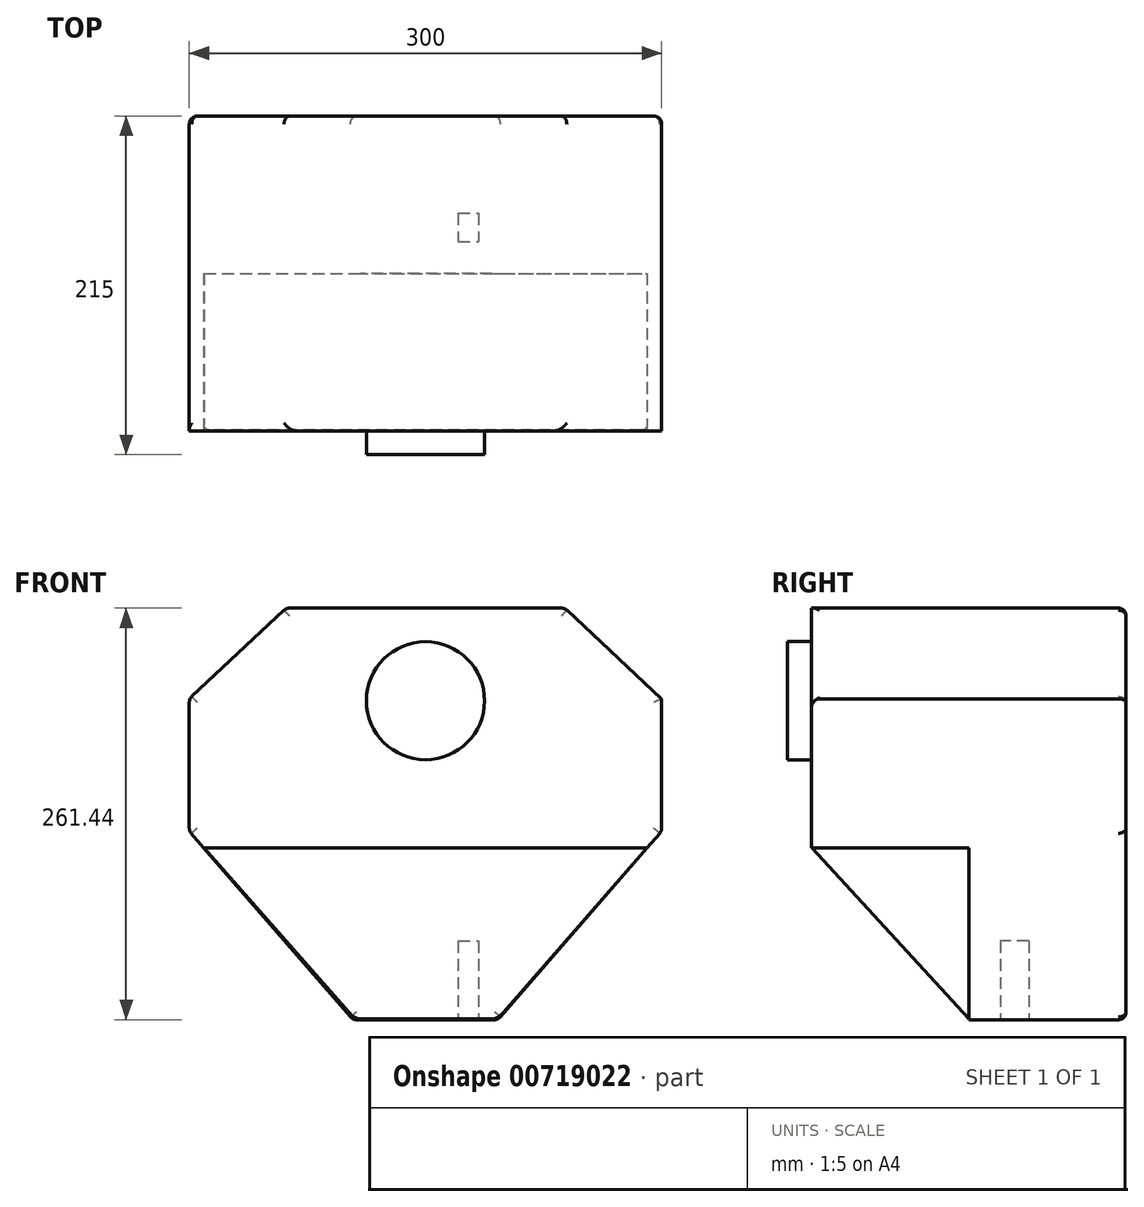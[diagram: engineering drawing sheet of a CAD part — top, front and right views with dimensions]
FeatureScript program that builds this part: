
annotation { "Feature Type Name" : "Feature", "Feature Type Description" : "" }
export const myFeature = defineFeature(function(context is Context, id is Id, definition is map)
    precondition{}
    {
        {
            var Q0;
            Q0=qCreatedBy(makeId("Front.planeOp"),FACE);
            var sketch = newSketch(context, id + "F0", { "sketchPlane" : qUnion([Q0])});
            skLineSegment(sketch, "E0.bottom", {"start": v(-150, -42) * mm, "end": v(150, -42) * mm});
            skLineSegment(sketch, "E0.top", {"start": v(-150, 42) * mm, "end": v(150, 42) * mm});
            skLineSegment(sketch, "E0.left", {"start": v(-150, -42) * mm, "end": v(-150, 42) * mm});
            skLineSegment(sketch, "E0.right", {"start": v(150, -42) * mm, "end": v(150, 42) * mm});
            skPoint(sketch, "E0.middle", {"position": v(0, 0) * mm});
            skLineSegment(sketch, "E1.bottom", {"start": v(-88.3, -15.66) * mm, "end": v(88.3, -15.66) * mm});
            skLineSegment(sketch, "E1.top", {"start": v(-88.3, 99.65) * mm, "end": v(88.3, 99.65) * mm});
            skLineSegment(sketch, "E1.left", {"start": v(-88.3, -15.66) * mm, "end": v(-88.3, 99.65) * mm});
            skLineSegment(sketch, "E1.right", {"start": v(88.3, -15.66) * mm, "end": v(88.3, 99.65) * mm});
            skPoint(sketch, "E1.middle", {"position": v(0, 42) * mm});
            skLineSegment(sketch, "E2.bottom", {"start": v(-46.14, -161.8) * mm, "end": v(46.14, -161.8) * mm});
            skLineSegment(sketch, "E2.top", {"start": v(-46.14, 77.8) * mm, "end": v(46.14, 77.8) * mm});
            skLineSegment(sketch, "E2.left", {"start": v(-46.14, -161.8) * mm, "end": v(-46.14, 77.8) * mm});
            skLineSegment(sketch, "E2.right", {"start": v(46.14, -161.8) * mm, "end": v(46.14, 77.8) * mm});
            skPoint(sketch, "E2.middle", {"position": v(0, -42) * mm});
            skLineSegment(sketch, "E3", {"start": v(-150, -42) * mm, "end": v(-46.14, -161.8) * mm});
            skLineSegment(sketch, "E4", {"start": v(46.14, -161.8) * mm, "end": v(150, -42) * mm});
            skLineSegment(sketch, "E5", {"start": v(-150, 42) * mm, "end": v(-88.3, 99.65) * mm});
            skLineSegment(sketch, "E6", {"start": v(150, 42) * mm, "end": v(88.3, 99.65) * mm});
            skSolve(sketch);
        }
        {
            var Q0;
            {var subQ0=sQuery(id+"F0.wireOp",EDGE,"E2.left");var subQ1=sQuery(id+"F0.wireOp",EDGE,"E0.top");var subQ2=makeQuery(id+"F0.imprint","INTERSECT",VERTEX,{"derivedFrom":[subQ1,subQ0]});Q0=makeQuery(id+"F0.imprint","IMPRINT",FACE,{"disambiguationData":[TD([[makeQuery(id+"F0.imprint","IMPRINT",EDGE,{"disambiguationData":[TD([[subQ2,-1.0]])],"derivedFrom":subQ1}),-1.0]])]});}
            var Q1;
            {var subQ0=sQuery(id+"F0.wireOp",EDGE,"E1.left");var subQ1=sQuery(id+"F0.wireOp",EDGE,"E0.top");var subQ2=makeQuery(id+"F0.imprint","INTERSECT",VERTEX,{"derivedFrom":[subQ1,subQ0]});Q1=makeQuery(id+"F0.imprint","IMPRINT",FACE,{"disambiguationData":[TD([[makeQuery(id+"F0.imprint","IMPRINT",EDGE,{"disambiguationData":[TD([[subQ2,-1.0]])],"derivedFrom":subQ1}),-1.0]])]});}
            var Q2;
            {var subQ0=sQuery(id+"F0.wireOp",EDGE,"E0.left");Q2=makeQuery(id+"F0.imprint","IMPRINT",FACE,{"disambiguationData":[TD([[makeQuery(id+"F0.imprint","IMPRINT",EDGE,{"derivedFrom":subQ0}),-1.0]])]});}
            var Q3;
            {var subQ0=sQuery(id+"F0.wireOp",EDGE,"E2.left");var subQ1=sQuery(id+"F0.wireOp",EDGE,"E0.bottom");var subQ2=makeQuery(id+"F0.imprint","INTERSECT",VERTEX,{"derivedFrom":[subQ1,subQ0]});Q3=makeQuery(id+"F0.imprint","IMPRINT",FACE,{"disambiguationData":[TD([[makeQuery(id+"F0.imprint","IMPRINT",EDGE,{"disambiguationData":[TD([[subQ2,-1.0]])],"derivedFrom":subQ1}),1.0]])]});}
            var Q4;
            {var subQ0=sQuery(id+"F0.wireOp",EDGE,"E0.right");Q4=makeQuery(id+"F0.imprint","IMPRINT",FACE,{"disambiguationData":[TD([[makeQuery(id+"F0.imprint","IMPRINT",EDGE,{"derivedFrom":subQ0}),1.0]])]});}
            var Q5;
            {var subQ0=sQuery(id+"F0.wireOp",EDGE,"E2.right");var subQ1=sQuery(id+"F0.wireOp",EDGE,"E0.top");var subQ2=makeQuery(id+"F0.imprint","INTERSECT",VERTEX,{"derivedFrom":[subQ1,subQ0]});Q5=makeQuery(id+"F0.imprint","IMPRINT",FACE,{"disambiguationData":[TD([[makeQuery(id+"F0.imprint","IMPRINT",EDGE,{"disambiguationData":[TD([[subQ2,-1.0]])],"derivedFrom":subQ1}),-1.0]])]});}
            var Q6;
            {var subQ0=sQuery(id+"F0.wireOp",EDGE,"E3");Q6=makeQuery(id+"F0.imprint","IMPRINT",FACE,{"disambiguationData":[TD([[makeQuery(id+"F0.imprint","IMPRINT",EDGE,{"derivedFrom":subQ0}),1.0]])]});}
            var Q7;
            {var subQ5=sQuery(id+"F0.wireOp",EDGE,"E2.bottom");Q7=makeQuery(id+"F0.imprint","IMPRINT",FACE,{"disambiguationData":[TD([[makeQuery(id+"F0.imprint","IMPRINT",EDGE,{"derivedFrom":subQ5}),1.0]])]});}
            var Q8;
            {var subQ0=sQuery(id+"F0.wireOp",EDGE,"E4");Q8=makeQuery(id+"F0.imprint","IMPRINT",FACE,{"disambiguationData":[TD([[makeQuery(id+"F0.imprint","IMPRINT",EDGE,{"derivedFrom":subQ0}),1.0]])]});}
            var Q9;
            {var subQ1=sQuery(id+"F0.wireOp",EDGE,"E1.top");Q9=makeQuery(id+"F0.imprint","IMPRINT",FACE,{"disambiguationData":[TD([[makeQuery(id+"F0.imprint","IMPRINT",EDGE,{"derivedFrom":subQ1}),-1.0]])]});}
            var Q10;
            {var subQ5=sQuery(id+"F0.wireOp",EDGE,"E2.top");Q10=makeQuery(id+"F0.imprint","IMPRINT",FACE,{"disambiguationData":[TD([[makeQuery(id+"F0.imprint","IMPRINT",EDGE,{"derivedFrom":subQ5}),-1.0]])]});}
            var Q11;
            {var subQ0=sQuery(id+"F0.wireOp",EDGE,"E5");Q11=makeQuery(id+"F0.imprint","IMPRINT",FACE,{"disambiguationData":[TD([[makeQuery(id+"F0.imprint","IMPRINT",EDGE,{"derivedFrom":subQ0}),-1.0]])]});}
            var Q12;
            {var subQ0=sQuery(id+"F0.wireOp",EDGE,"E6");Q12=makeQuery(id+"F0.imprint","IMPRINT",FACE,{"disambiguationData":[TD([[makeQuery(id+"F0.imprint","IMPRINT",EDGE,{"derivedFrom":subQ0}),1.0]])]});}
            extrude(context, id + "F1", {"entities" : qUnion([Q0, Q1, Q2, Q3, Q4, Q5, Q6, Q7, Q8, Q9, Q10, Q11, Q12]), "depth" : 100 * mm, "offsetDistance" : 25 * mm, "hasSecondDirection" : true, "secondDirectionOppositeDirection" : true, "secondDirectionDepth" : 100 * mm});
        }
        {
            var Q0;
            Q0=makeQuery(id+"F1.opExtrude","CAP_FACE",FACE,{"disambiguationData":[OSD([sQuery(id+"F0.wireOp",EDGE,"E0.left"),sQuery(id+"F0.wireOp",EDGE,"E0.right"),sQuery(id+"F0.wireOp",EDGE,"E1.top"),sQuery(id+"F0.wireOp",EDGE,"E2.bottom"),sQuery(id+"F0.wireOp",EDGE,"E3"),sQuery(id+"F0.wireOp",EDGE,"E4"),sQuery(id+"F0.wireOp",EDGE,"E5"),sQuery(id+"F0.wireOp",EDGE,"E6")])],"isStart":false});
            var sketch = newSketch(context, id + "F2", { "sketchPlane" : qUnion([Q0])});
            skLineSegment(sketch, "E7", {"start": v(-140.78, -52.63) * mm, "end": v(140.78, -52.63) * mm});
            skLineSegment(sketch, "E8", {"start": v(140.78, -52.63) * mm, "end": v(46.14, -161.8) * mm});
            skLineSegment(sketch, "E9", {"start": v(46.14, -161.8) * mm, "end": v(-46.14, -161.8) * mm});
            skLineSegment(sketch, "E10", {"start": v(-46.14, -161.8) * mm, "end": v(-140.78, -52.63) * mm});
            skSolve(sketch);
        }
        {
            var Q0;
            Q0 = qSketchRegion(id + "F2", true);
            extrude(context, id + "F3", {"entities" : qUnion([Q0]), "operationType" : NewBodyOperationType.REMOVE, "oppositeDirection" : true, "depth" : 100 * mm, "offsetDistance" : 25 * mm});
        }
        {
            var Q0;
            Q0=qCreatedBy(makeId("Right.planeOp"),FACE);
            var sketch = newSketch(context, id + "F4", { "sketchPlane" : qUnion([Q0])});
            skLineSegment(sketch, "E11", {"start": v(0, -161.34) * mm, "end": v(-99.62, -52.57) * mm});
            skLineSegment(sketch, "E12", {"start": v(-99.62, -52.57) * mm, "end": v(0, -52.57) * mm});
            skLineSegment(sketch, "E13", {"start": v(0, -52.57) * mm, "end": v(0, -161.34) * mm});
            skSolve(sketch);
        }
        {
            var Q0;
            Q0=makeQuery(id+"F4.imprint","IMPRINT",FACE,{"disambiguationData":[TD([[makeQuery(id+"F4.imprint","IMPRINT",EDGE,{"derivedFrom":sQuery(id+"F4.wireOp",EDGE,"E11")}),-1.0]])]});
            extrude(context, id + "F5", {"entities" : qUnion([Q0]), "operationType" : NewBodyOperationType.ADD, "depth" : 150 * mm, "offsetDistance" : 25 * mm, "hasSecondDirection" : true, "secondDirectionOppositeDirection" : true, "secondDirectionDepth" : 150 * mm});
        }
        {
            var Q0;
            Q0=makeQuery(id+"F1.opExtrude","CAP_FACE",FACE,{"disambiguationData":[OSD([sQuery(id+"F0.wireOp",EDGE,"E0.left"),sQuery(id+"F0.wireOp",EDGE,"E0.right"),sQuery(id+"F0.wireOp",EDGE,"E1.top"),sQuery(id+"F0.wireOp",EDGE,"E2.bottom"),sQuery(id+"F0.wireOp",EDGE,"E3"),sQuery(id+"F0.wireOp",EDGE,"E4"),sQuery(id+"F0.wireOp",EDGE,"E5"),sQuery(id+"F0.wireOp",EDGE,"E6")])],"isStart":false});
            var sketch = newSketch(context, id + "F6", { "sketchPlane" : qUnion([Q0])});
            skLineSegment(sketch, "E14", {"start": v(-150, -42) * mm, "end": v(-44.71, -161.7) * mm});
            skLineSegment(sketch, "E15", {"start": v(-44.71, -161.7) * mm, "end": v(45.6, -161.7) * mm});
            skLineSegment(sketch, "E16", {"start": v(45.6, -161.7) * mm, "end": v(150, -42) * mm});
            skLineSegment(sketch, "E17", {"start": v(150, -42) * mm, "end": v(150, -161.7) * mm});
            skLineSegment(sketch, "E18", {"start": v(150, -161.7) * mm, "end": v(-150.56, -161.7) * mm});
            skLineSegment(sketch, "E19", {"start": v(-150.56, -161.7) * mm, "end": v(-150, -42) * mm});
            skSolve(sketch);
        }
        {
            var Q0;
            {var subQ1=sQuery(id+"F6.wireOp",EDGE,"E19");Q0=makeQuery(id+"F6.imprint","IMPRINT",FACE,{"disambiguationData":[TD([[makeQuery(id+"F6.imprint","IMPRINT",EDGE,{"derivedFrom":subQ1}),-1.0]])]});}
            var Q1;
            {var subQ1=sQuery(id+"F6.wireOp",EDGE,"E17");Q1=makeQuery(id+"F6.imprint","IMPRINT",FACE,{"disambiguationData":[TD([[makeQuery(id+"F6.imprint","IMPRINT",EDGE,{"derivedFrom":subQ1}),-1.0]])]});}
            extrude(context, id + "F7", {"entities" : qUnion([Q0, Q1]), "operationType" : NewBodyOperationType.REMOVE, "oppositeDirection" : true, "depth" : 100 * mm, "offsetDistance" : 25 * mm});
        }
        {
            var Q0;
            Q0=makeQuery(id+"F1.opExtrude","CAP_EDGE",EDGE,{"disambiguationData":[OSD([sQuery(id+"F0.wireOp",EDGE,"E1.top")])],"isStart":true});
            var Q1;
            Q1=makeQuery(id+"F1.opExtrude","CAP_EDGE",EDGE,{"disambiguationData":[OSD([sQuery(id+"F0.wireOp",EDGE,"E6")])],"isStart":true});
            var Q2;
            Q2=makeQuery(id+"F1.opExtrude","CAP_FACE",FACE,{"disambiguationData":[OSD([sQuery(id+"F0.wireOp",EDGE,"E0.left"),sQuery(id+"F0.wireOp",EDGE,"E0.right"),sQuery(id+"F0.wireOp",EDGE,"E1.top"),sQuery(id+"F0.wireOp",EDGE,"E2.bottom"),sQuery(id+"F0.wireOp",EDGE,"E3"),sQuery(id+"F0.wireOp",EDGE,"E4"),sQuery(id+"F0.wireOp",EDGE,"E5"),sQuery(id+"F0.wireOp",EDGE,"E6")])],"isStart":true});
            fillet(context, id + "F8", {"entities" : qUnion([Q0, Q1, Q2]), "radius" : 5 * mm, "tangentPropagation" : true, "allowEdgeOverflow" : false});
        }
        {
            var Q0;
            Q0=makeQuery(id+"F1.opExtrude","SWEPT_EDGE",EDGE,{"disambiguationData":[OSD([sQuery(id+"F0.wireOp",EDGE,"E0.bottom"),sQuery(id+"F0.wireOp",EDGE,"E0.right"),sQuery(id+"F0.wireOp",EDGE,"E4")])]});
            var Q1;
            Q1=makeQuery(id+"F7.boolean.opBoolean","INTERSECT",EDGE,{"derivedFrom":[makeQuery(id+"F5.opExtrude","SWEPT_FACE",FACE,{"disambiguationData":[OSD([sQuery(id+"F4.wireOp",EDGE,"E11")])]}),makeQuery(id+"F7.opExtrude","SWEPT_FACE",FACE,{"disambiguationData":[OSD([sQuery(id+"F6.wireOp",EDGE,"E16")])]})]});
            var Q2;
            Q2=makeQuery(id+"F1.opExtrude","SWEPT_EDGE",EDGE,{"disambiguationData":[OSD([sQuery(id+"F0.wireOp",EDGE,"E2.bottom"),sQuery(id+"F0.wireOp",EDGE,"E2.right"),sQuery(id+"F0.wireOp",EDGE,"E4")])]});
            var Q3;
            Q3=makeQuery(id+"F1.opExtrude","CAP_EDGE",EDGE,{"disambiguationData":[OSD([sQuery(id+"F0.wireOp",EDGE,"E6")])],"isStart":false});
            var Q4;
            Q4=makeQuery(id+"F1.opExtrude","SWEPT_EDGE",EDGE,{"disambiguationData":[OSD([sQuery(id+"F0.wireOp",EDGE,"E1.top"),sQuery(id+"F0.wireOp",EDGE,"E1.right"),sQuery(id+"F0.wireOp",EDGE,"E6")])]});
            var Q5;
            Q5=makeQuery(id+"F1.opExtrude","SWEPT_EDGE",EDGE,{"disambiguationData":[OSD([sQuery(id+"F0.wireOp",EDGE,"E1.top"),sQuery(id+"F0.wireOp",EDGE,"E1.left"),sQuery(id+"F0.wireOp",EDGE,"E5")])]});
            var Q6;
            Q6=makeQuery(id+"F1.opExtrude","CAP_EDGE",EDGE,{"disambiguationData":[OSD([sQuery(id+"F0.wireOp",EDGE,"E5")])],"isStart":false});
            var Q7;
            Q7=makeQuery(id+"F1.opExtrude","SWEPT_EDGE",EDGE,{"disambiguationData":[OSD([sQuery(id+"F0.wireOp",EDGE,"E0.top"),sQuery(id+"F0.wireOp",EDGE,"E0.left"),sQuery(id+"F0.wireOp",EDGE,"E5")])]});
            var Q8;
            Q8=makeQuery(id+"F1.opExtrude","SWEPT_EDGE",EDGE,{"disambiguationData":[OSD([sQuery(id+"F0.wireOp",EDGE,"E0.bottom"),sQuery(id+"F0.wireOp",EDGE,"E0.left"),sQuery(id+"F0.wireOp",EDGE,"E3")])]});
            var Q9;
            Q9=makeQuery(id+"F7.boolean.opBoolean","INTERSECT",EDGE,{"derivedFrom":[makeQuery(id+"F5.opExtrude","SWEPT_FACE",FACE,{"disambiguationData":[OSD([sQuery(id+"F4.wireOp",EDGE,"E11")])]}),makeQuery(id+"F7.opExtrude","SWEPT_FACE",FACE,{"disambiguationData":[OSD([sQuery(id+"F6.wireOp",EDGE,"E14")])]})]});
            var Q10;
            Q10=makeQuery(id+"F1.opExtrude","SWEPT_EDGE",EDGE,{"disambiguationData":[OSD([sQuery(id+"F0.wireOp",EDGE,"E2.bottom"),sQuery(id+"F0.wireOp",EDGE,"E2.left"),sQuery(id+"F0.wireOp",EDGE,"E3")])]});
            fillet(context, id + "F9", {"entities" : qUnion([Q0, Q1, Q2, Q3, Q4, Q5, Q6, Q7, Q8, Q9, Q10]), "radius" : 5 * mm, "tangentPropagation" : true, "allowEdgeOverflow" : false});
        }
        {
            var Q0;
            Q0=makeQuery(id+"F1.opExtrude","CAP_FACE",FACE,{"disambiguationData":[OSD([sQuery(id+"F0.wireOp",EDGE,"E0.left"),sQuery(id+"F0.wireOp",EDGE,"E0.right"),sQuery(id+"F0.wireOp",EDGE,"E1.top"),sQuery(id+"F0.wireOp",EDGE,"E2.bottom"),sQuery(id+"F0.wireOp",EDGE,"E3"),sQuery(id+"F0.wireOp",EDGE,"E4"),sQuery(id+"F0.wireOp",EDGE,"E5"),sQuery(id+"F0.wireOp",EDGE,"E6")])],"isStart":false});
            var sketch = newSketch(context, id + "F10", { "sketchPlane" : qUnion([Q0])});
            skCircle(sketch, "E20", {"center": v(0, 40.8) * mm, "radius": 37.5 * mm});
            skPoint(sketch, "E20.centerSnap0", {"position": v(0, -52.63) * mm});
            skSolve(sketch);
        }
        {
            var Q0;
            Q0=makeQuery(id+"F10.imprint","IMPRINT",FACE,{"disambiguationData":[TD([[makeQuery(id+"F10.imprint","IMPRINT",EDGE,{"derivedFrom":sQuery(id+"F10.wireOp",EDGE,"E20")}),1.0]])]});
            var Q1;
            Q1=sQuery(id+"F10.wireOp",EDGE,"E20");
            extrude(context, id + "F11", {"entities" : qUnion([Q0]), "operationType" : NewBodyOperationType.ADD, "surfaceEntities" : qUnion([Q1]), "depth" : 15 * mm, "offsetDistance" : 25 * mm});
        }
        {
            var Q0;
            Q0=makeQuery(id+"F1.opExtrude","SWEPT_FACE",FACE,{"disambiguationData":[OSD([sQuery(id+"F0.wireOp",EDGE,"E2.bottom")])]});
            var sketch = newSketch(context, id + "F12", { "sketchPlane" : qUnion([Q0])});
            skLineSegment(sketch, "E21.bottom", {"start": v(20.82, -38.24) * mm, "end": v(33.67, -38.24) * mm});
            skLineSegment(sketch, "E21.top", {"start": v(20.82, -20.25) * mm, "end": v(33.67, -20.25) * mm});
            skLineSegment(sketch, "E21.left", {"start": v(20.82, -38.24) * mm, "end": v(20.82, -20.25) * mm});
            skLineSegment(sketch, "E21.right", {"start": v(33.67, -38.24) * mm, "end": v(33.67, -20.25) * mm});
            skPoint(sketch, "E21.middle", {"position": v(27.24, -29.25) * mm});
            skSolve(sketch);
        }
        {
            var Q0;
            Q0 = qSketchRegion(id + "F12", true);
            extrude(context, id + "F13", {"entities" : qUnion([Q0]), "operationType" : NewBodyOperationType.REMOVE, "oppositeDirection" : true, "depth" : 50 * mm, "offsetDistance" : 25 * mm});
        }
    });
